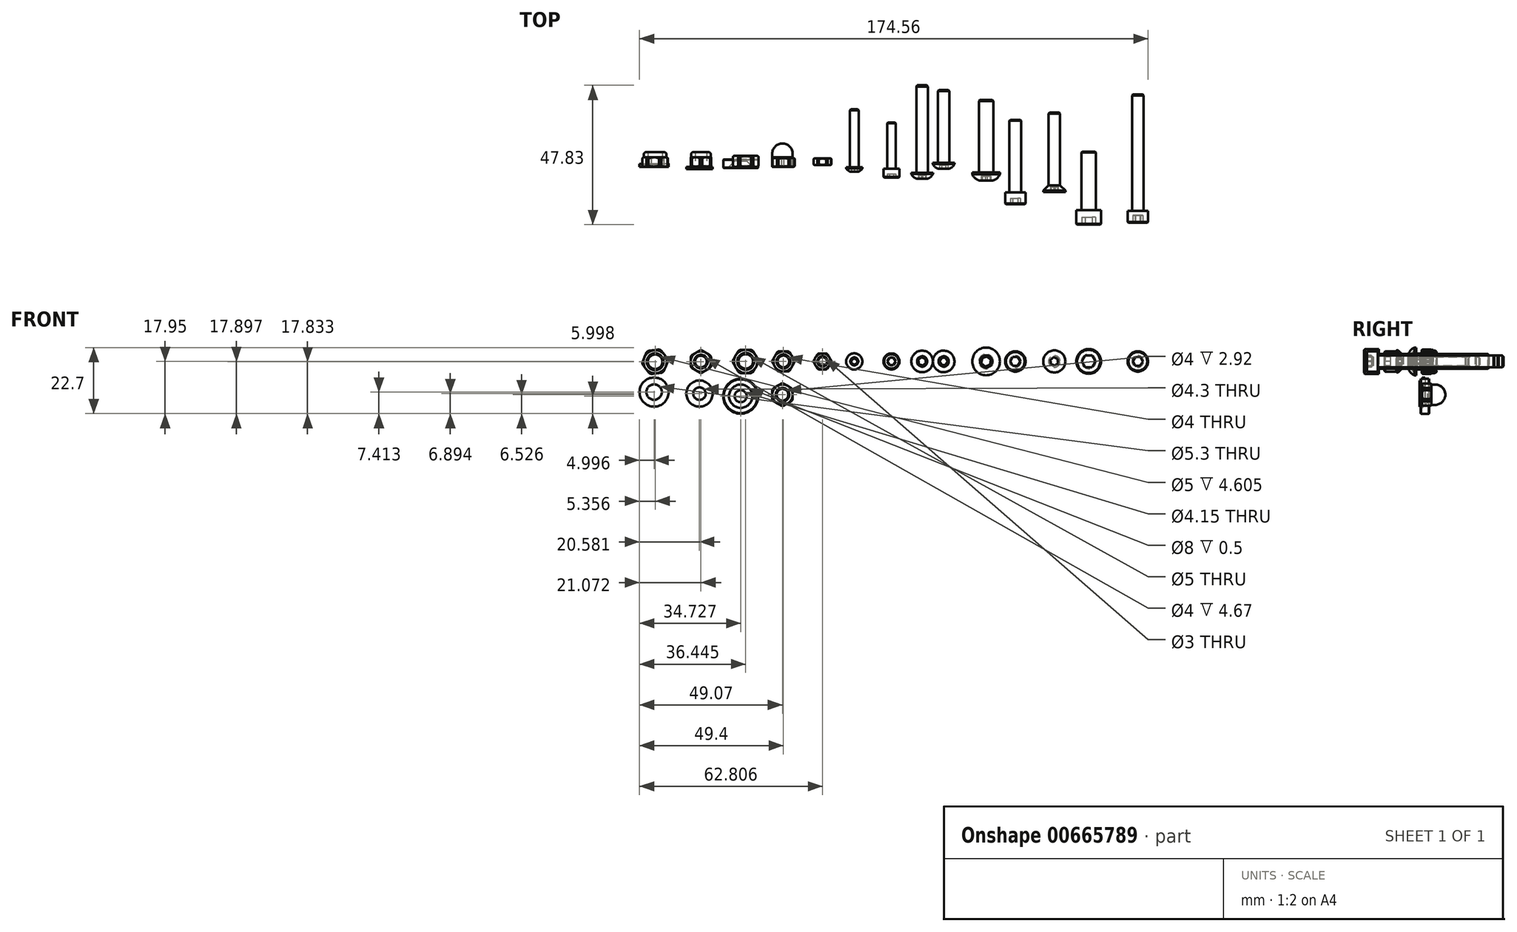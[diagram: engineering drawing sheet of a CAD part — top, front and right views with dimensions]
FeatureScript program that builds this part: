
annotation { "Feature Type Name" : "Feature", "Feature Type Description" : "" }
export const myFeature = defineFeature(function(context is Context, id is Id, definition is map)
    precondition{}
    {
        {
            var Q0;
            Q0=qCreatedBy(makeId("Top.planeOp"),FACE);
            var sketch = newSketch(context, id + "F0", { "sketchPlane" : qUnion([Q0])});
            skLineSegment(sketch, "E0.bottom", {"start": v(-2, 0) * mm, "end": v(-3.83, 0) * mm});
            skLineSegment(sketch, "E0.top", {"start": v(-2, 3) * mm, "end": v(-3.83, 3) * mm});
            skLineSegment(sketch, "E0.left", {"start": v(-2, 0) * mm, "end": v(-2, 3) * mm});
            skLineSegment(sketch, "E0.right", {"start": v(-3.83, 0) * mm, "end": v(-3.83, 3) * mm});
            skLineSegment(sketch, "E1", {"start": v(-2, 0) * mm, "end": v(0, 0) * mm, "construction": true});
            skLineSegment(sketch, "E2", {"start": v(0, 0) * mm, "end": v(0, 3) * mm, "construction": true});
            skSolve(sketch);
        }
        {
            var Q0;
            Q0=qSketchRegion(id+"F0",true);
            var Q1;
            Q1=sQuery(id+"F0.wireOp",EDGE,"E2");
            revolve(context, id + "F1", {"entities" : qUnion([Q0]), "axis" : qUnion([Q1]), "revolveType" : RevolveType.FULL});
        }
        {
            var Q0;
            Q0=makeQuery(id+"F1.opRevolve","SWEPT_EDGE",EDGE,{"disambiguationData":[OSD([sQuery(id+"F0.wireOp",EDGE,"E0.bottom"),sQuery(id+"F0.wireOp",EDGE,"E0.right")])]});
            var Q1;
            Q1=makeQuery(id+"F1.opRevolve","SWEPT_EDGE",EDGE,{"disambiguationData":[OSD([sQuery(id+"F0.wireOp",EDGE,"E0.top"),sQuery(id+"F0.wireOp",EDGE,"E0.right")])]});
            var Q2;
            Q2=makeQuery(id+"F1.opRevolve","SWEPT_EDGE",EDGE,{"disambiguationData":[OSD([sQuery(id+"F0.wireOp",EDGE,"E0.bottom"),sQuery(id+"F0.wireOp",EDGE,"E0.left")])]});
            var Q3;
            Q3=makeQuery(id+"F1.opRevolve","SWEPT_EDGE",EDGE,{"disambiguationData":[OSD([sQuery(id+"F0.wireOp",EDGE,"E0.top"),sQuery(id+"F0.wireOp",EDGE,"E0.left")])]});
            chamfer(context, id + "F2", {"entities" : qUnion([Q0, Q1, Q2, Q3]), "chamferType" : ChamferType.OFFSET_ANGLE, "width" : 0.77 * mm / 2, "oppositeDirection" : false, "angle" : 30 * degree, "tangentPropagation" : true});
        }
        {
            var Q0;
            Q0=makeQuery(id+"F1.opRevolve","SWEPT_FACE",FACE,{"disambiguationData":[OSD([sQuery(id+"F0.wireOp",EDGE,"E0.bottom")])]});
            var sketch = newSketch(context, id + "F3", { "sketchPlane" : qUnion([Q0])});
            skCircle(sketch, "E3.cCircle", {"center": v(0, 0) * mm, "radius": 3.45 * mm, "construction": true});
            skLineSegment(sketch, "E3.0", {"start": v(3.98, 0) * mm, "end": v(2, -3.45) * mm});
            skLineSegment(sketch, "E3.1", {"start": v(2, -3.45) * mm, "end": v(-2, -3.45) * mm});
            skLineSegment(sketch, "E3.2", {"start": v(-2, -3.45) * mm, "end": v(-3.98, 0) * mm});
            skLineSegment(sketch, "E3.3", {"start": v(-3.98, 0) * mm, "end": v(-2, 3.45) * mm});
            skLineSegment(sketch, "E3.4", {"start": v(-2, 3.45) * mm, "end": v(2, 3.45) * mm});
            skLineSegment(sketch, "E3.5", {"start": v(2, 3.45) * mm, "end": v(3.98, 0) * mm});
            skPoint(sketch, "E3.0.midPoint", {"position": v(2.99, -1.73) * mm});
            skCircle(sketch, "E4", {"center": v(0, 0) * mm, "radius": 4.53 * mm});
            skSolve(sketch);
        }
        {
            var Q0;
            Q0=qSketchRegion(id+"F3",true);
            extrude(context, id + "F4", {"entities" : qUnion([Q0]), "operationType" : NewBodyOperationType.REMOVE, "oppositeDirection" : true, "depth" : 25 * mm, "offsetDistance" : 25 * mm});
        }
        {
            var Q0;
            Q0=qCreatedBy(makeId("Top.planeOp"),FACE);
            var sketch = newSketch(context, id + "F5", { "sketchPlane" : qUnion([Q0])});
            skLineSegment(sketch, "E5.bottom", {"start": v(10.4, 2.85) * mm, "end": v(11.9, 2.85) * mm});
            skLineSegment(sketch, "E5.top", {"start": v(10.4, 0.58) * mm, "end": v(11.9, 0.58) * mm});
            skLineSegment(sketch, "E5.left", {"start": v(10.4, 2.85) * mm, "end": v(10.4, 0.58) * mm});
            skLineSegment(sketch, "E5.right", {"start": v(11.9, 2.85) * mm, "end": v(11.9, 0.58) * mm});
            skLineSegment(sketch, "E6", {"start": v(11.9, 0.58) * mm, "end": v(13.4, 0.58) * mm, "construction": true});
            skLineSegment(sketch, "E7", {"start": v(13.4, 0.58) * mm, "end": v(13.4, 2.85) * mm, "construction": true});
            skSolve(sketch);
        }
        {
            var Q0;
            Q0=qSketchRegion(id+"F5",true);
            var Q1;
            Q1=sQuery(id+"F5.wireOp",EDGE,"E7");
            revolve(context, id + "F6", {"entities" : qUnion([Q0]), "axis" : qUnion([Q1]), "revolveType" : RevolveType.FULL});
        }
        {
            var Q0;
            Q0=makeQuery(id+"F6.opRevolve","SWEPT_EDGE",EDGE,{"disambiguationData":[OSD([sQuery(id+"F5.wireOp",EDGE,"E5.top"),sQuery(id+"F5.wireOp",EDGE,"E5.right")])]});
            var Q1;
            Q1=makeQuery(id+"F6.opRevolve","SWEPT_EDGE",EDGE,{"disambiguationData":[OSD([sQuery(id+"F5.wireOp",EDGE,"E5.top"),sQuery(id+"F5.wireOp",EDGE,"E5.left")])]});
            var Q2;
            Q2=makeQuery(id+"F6.opRevolve","SWEPT_EDGE",EDGE,{"disambiguationData":[OSD([sQuery(id+"F5.wireOp",EDGE,"E5.bottom"),sQuery(id+"F5.wireOp",EDGE,"E5.right")])]});
            var Q3;
            Q3=makeQuery(id+"F6.opRevolve","SWEPT_EDGE",EDGE,{"disambiguationData":[OSD([sQuery(id+"F5.wireOp",EDGE,"E5.bottom"),sQuery(id+"F5.wireOp",EDGE,"E5.left")])]});
            chamfer(context, id + "F7", {"entities" : qUnion([Q0, Q1, Q2, Q3]), "width" : 0.51 / 2 * mm, "tangentPropagation" : true});
        }
        {
            var Q0;
            Q0=makeQuery(id+"F6.opRevolve","SWEPT_FACE",FACE,{"disambiguationData":[OSD([sQuery(id+"F5.wireOp",EDGE,"E5.top")])]});
            var sketch = newSketch(context, id + "F8", { "sketchPlane" : qUnion([Q0])});
            skCircle(sketch, "E8.cCircle", {"center": v(13.4, 0) * mm, "radius": 2.75 * mm, "construction": true});
            skLineSegment(sketch, "E8.0", {"start": v(16.58, 0) * mm, "end": v(15, -2.75) * mm});
            skLineSegment(sketch, "E8.1", {"start": v(15, -2.75) * mm, "end": v(11.82, -2.75) * mm});
            skLineSegment(sketch, "E8.2", {"start": v(11.82, -2.75) * mm, "end": v(10.23, 0) * mm});
            skLineSegment(sketch, "E8.3", {"start": v(10.23, 0) * mm, "end": v(11.82, 2.75) * mm});
            skLineSegment(sketch, "E8.4", {"start": v(11.82, 2.75) * mm, "end": v(15, 2.75) * mm});
            skLineSegment(sketch, "E8.5", {"start": v(15, 2.75) * mm, "end": v(16.58, 0) * mm});
            skPoint(sketch, "E8.0.midPoint", {"position": v(15.79, -1.38) * mm});
            skCircle(sketch, "E9", {"center": v(13.4, 0) * mm, "radius": 3.66 * mm});
            skSolve(sketch);
        }
        {
            var Q0;
            Q0=qSketchRegion(id+"F8",true);
            extrude(context, id + "F9", {"entities" : qUnion([Q0]), "operationType" : NewBodyOperationType.REMOVE, "oppositeDirection" : true, "depth" : 25 * mm, "offsetDistance" : 25 * mm});
        }
        {
            var Q0;
            Q0=qCreatedBy(makeId("Top.planeOp"),FACE);
            var sketch = newSketch(context, id + "F10", { "sketchPlane" : qUnion([Q0])});
            skLineSegment(sketch, "E10.bottom", {"start": v(-15.45, 3.8) * mm, "end": v(-17.35, 3.8) * mm});
            skLineSegment(sketch, "E10.top", {"start": v(-15.45, -0.05) * mm, "end": v(-17.35, -0.05) * mm});
            skLineSegment(sketch, "E10.left", {"start": v(-15.45, 3.8) * mm, "end": v(-15.45, -0.05) * mm});
            skLineSegment(sketch, "E10.right", {"start": v(-17.35, 3.8) * mm, "end": v(-17.35, -0.05) * mm});
            skLineSegment(sketch, "E11", {"start": v(-15.45, 3.8) * mm, "end": v(-12.95, 3.8) * mm, "construction": true});
            skLineSegment(sketch, "E12", {"start": v(-12.95, 3.8) * mm, "end": v(-12.95, -0.05) * mm, "construction": true});
            skSolve(sketch);
        }
        {
            var Q0;
            Q0=qSketchRegion(id+"F10",true);
            var Q1;
            Q1=sQuery(id+"F10.wireOp",EDGE,"E12");
            revolve(context, id + "F11", {"entities" : qUnion([Q0]), "axis" : qUnion([Q1]), "revolveType" : RevolveType.FULL});
        }
        {
            var Q0;
            Q0=makeQuery(id+"F11.opRevolve","SWEPT_EDGE",EDGE,{"disambiguationData":[OSD([sQuery(id+"F10.wireOp",EDGE,"E10.bottom"),sQuery(id+"F10.wireOp",EDGE,"E10.left")])]});
            var Q1;
            Q1=makeQuery(id+"F11.opRevolve","SWEPT_EDGE",EDGE,{"disambiguationData":[OSD([sQuery(id+"F10.wireOp",EDGE,"E10.bottom"),sQuery(id+"F10.wireOp",EDGE,"E10.right")])]});
            var Q2;
            Q2=makeQuery(id+"F11.opRevolve","SWEPT_EDGE",EDGE,{"disambiguationData":[OSD([sQuery(id+"F10.wireOp",EDGE,"E10.top"),sQuery(id+"F10.wireOp",EDGE,"E10.left")])]});
            var Q3;
            Q3=makeQuery(id+"F11.opRevolve","SWEPT_EDGE",EDGE,{"disambiguationData":[OSD([sQuery(id+"F10.wireOp",EDGE,"E10.top"),sQuery(id+"F10.wireOp",EDGE,"E10.right")])]});
            chamfer(context, id + "F12", {"entities" : qUnion([Q0, Q1, Q2, Q3]), "width" : 0.4 * mm, "tangentPropagation" : true});
        }
        {
            var Q0;
            Q0=makeQuery(id+"F11.opRevolve","SWEPT_FACE",FACE,{"disambiguationData":[OSD([sQuery(id+"F10.wireOp",EDGE,"E10.top")])]});
            var sketch = newSketch(context, id + "F13", { "sketchPlane" : qUnion([Q0])});
            skCircle(sketch, "E13.cCircle", {"center": v(-12.95, 0) * mm, "radius": 4 * mm, "construction": true});
            skLineSegment(sketch, "E13.0", {"start": v(-8.34, 0) * mm, "end": v(-10.65, -4) * mm});
            skLineSegment(sketch, "E13.1", {"start": v(-10.65, -4) * mm, "end": v(-15.26, -4) * mm});
            skLineSegment(sketch, "E13.2", {"start": v(-15.26, -4) * mm, "end": v(-17.57, 0) * mm});
            skLineSegment(sketch, "E13.3", {"start": v(-17.57, 0) * mm, "end": v(-15.26, 4) * mm});
            skLineSegment(sketch, "E13.4", {"start": v(-15.26, 4) * mm, "end": v(-10.65, 4) * mm});
            skLineSegment(sketch, "E13.5", {"start": v(-10.65, 4) * mm, "end": v(-8.34, 0) * mm});
            skPoint(sketch, "E13.0.midPoint", {"position": v(-9.5, -2) * mm});
            skCircle(sketch, "E14", {"center": v(-12.95, 0) * mm, "radius": 5.32 * mm});
            skSolve(sketch);
        }
        {
            var Q0;
            Q0=qSketchRegion(id+"F13",true);
            extrude(context, id + "F14", {"entities" : qUnion([Q0]), "operationType" : NewBodyOperationType.REMOVE, "oppositeDirection" : true, "depth" : 25 * mm, "offsetDistance" : 25 * mm});
        }
        {
            var Q0;
            Q0=qCreatedBy(makeId("Top.planeOp"),FACE);
            var sketch = newSketch(context, id + "F15", { "sketchPlane" : qUnion([Q0])});
            skLineSegment(sketch, "E15", {"start": v(24.32, 19.82) * mm, "end": v(24.32, -1.7) * mm});
            skLineSegment(sketch, "E16", {"start": v(24.32, -1.7) * mm, "end": v(22.95, -1.7) * mm});
            skLineSegment(sketch, "E17", {"start": v(21.55, -0.58) * mm, "end": v(21.55, -0.18) * mm});
            skLineSegment(sketch, "E18", {"start": v(21.55, -0.18) * mm, "end": v(22.82, -0.18) * mm});
            skLineSegment(sketch, "E19", {"start": v(22.82, -0.18) * mm, "end": v(22.82, 19.41) * mm});
            skLineSegment(sketch, "E20", {"start": v(22.82, 19.41) * mm, "end": v(23.18, 19.82) * mm});
            skLineSegment(sketch, "E21", {"start": v(23.18, 19.82) * mm, "end": v(24.32, 19.82) * mm});
            skArc(sketch, "E22", {"start": v(22.95, -1.7) * mm, "mid": v(22.16, -1.26) * mm, "end": v(21.55, -0.58) * mm});
            skSolve(sketch);
        }
        {
            var Q0;
            Q0=qSketchRegion(id+"F15",true);
            var Q1;
            Q1=sQuery(id+"F15.wireOp",EDGE,"E15");
            revolve(context, id + "F16", {"entities" : qUnion([Q0]), "axis" : qUnion([Q1]), "revolveType" : RevolveType.FULL});
        }
        {
            var Q0;
            Q0=makeQuery(id+"F16.opRevolve","SWEPT_FACE",FACE,{"disambiguationData":[OSD([sQuery(id+"F15.wireOp",EDGE,"E16")])]});
            var sketch = newSketch(context, id + "F17", { "sketchPlane" : qUnion([Q0])});
            skCircle(sketch, "E23.cCircle", {"center": v(24.32, 0) * mm, "radius": 1.02 * mm, "construction": true});
            skLineSegment(sketch, "E23.0", {"start": v(25.34, 0.59) * mm, "end": v(25.34, -0.59) * mm});
            skLineSegment(sketch, "E23.1", {"start": v(25.34, -0.59) * mm, "end": v(24.32, -1.17) * mm});
            skLineSegment(sketch, "E23.2", {"start": v(24.32, -1.17) * mm, "end": v(23.3, -0.59) * mm});
            skLineSegment(sketch, "E23.3", {"start": v(23.3, -0.59) * mm, "end": v(23.3, 0.59) * mm});
            skLineSegment(sketch, "E23.4", {"start": v(23.3, 0.59) * mm, "end": v(24.32, 1.17) * mm});
            skLineSegment(sketch, "E23.5", {"start": v(24.32, 1.17) * mm, "end": v(25.34, 0.59) * mm});
            skPoint(sketch, "E23.0.midPoint", {"position": v(25.34, 0) * mm});
            skSolve(sketch);
        }
        {
            var Q0;
            Q0=qSketchRegion(id+"F17",true);
            extrude(context, id + "F18", {"entities" : qUnion([Q0]), "operationType" : NewBodyOperationType.REMOVE, "oppositeDirection" : true, "depth" : 1.04 * mm, "offsetDistance" : 25 * mm});
        }
        {
            var Q0;
            Q0=qCreatedBy(makeId("Top.planeOp"),FACE);
            var sketch = newSketch(context, id + "F19", { "sketchPlane" : qUnion([Q0])});
            skLineSegment(sketch, "E24.bottom", {"start": v(34.33, -0.72) * mm, "end": v(35.58, -0.72) * mm});
            skLineSegment(sketch, "E24.top", {"start": v(34.61, -3.72) * mm, "end": v(37.08, -3.72) * mm});
            skLineSegment(sketch, "E24.left", {"start": v(34.33, -0.72) * mm, "end": v(34.33, -3.44) * mm});
            skLineSegment(sketch, "E24.right", {"start": v(37.08, -0.72) * mm, "end": v(37.08, -3.72) * mm});
            skLineSegment(sketch, "E25.top", {"start": v(37.08, 15.2) * mm, "end": v(35.86, 15.2) * mm});
            skLineSegment(sketch, "E25.left", {"start": v(37.08, -0.72) * mm, "end": v(37.08, 15.2) * mm});
            skLineSegment(sketch, "E25.right", {"start": v(35.58, -0.72) * mm, "end": v(35.58, 14.92) * mm});
            skLineSegment(sketch, "E26", {"start": v(34.33, -3.44) * mm, "end": v(34.61, -3.72) * mm});
            skLineSegment(sketch, "E27", {"start": v(35.58, 14.92) * mm, "end": v(35.86, 15.2) * mm});
            skSolve(sketch);
        }
        {
            var Q0;
            Q0=qSketchRegion(id+"F19",true);
            var Q1;
            Q1=sQuery(id+"F19.wireOp",EDGE,"E25.left");
            revolve(context, id + "F20", {"entities" : qUnion([Q0]), "axis" : qUnion([Q1]), "revolveType" : RevolveType.FULL});
        }
        {
            var Q0;
            Q0=makeQuery(id+"F20.opRevolve","SWEPT_FACE",FACE,{"disambiguationData":[OSD([sQuery(id+"F19.wireOp",EDGE,"E24.top")])]});
            var sketch = newSketch(context, id + "F21", { "sketchPlane" : qUnion([Q0])});
            skCircle(sketch, "E28.cCircle", {"center": v(37.08, 0) * mm, "radius": 1.25 * mm, "construction": true});
            skLineSegment(sketch, "E28.0", {"start": v(37.8, 1.25) * mm, "end": v(38.52, 0) * mm});
            skLineSegment(sketch, "E28.1", {"start": v(38.52, 0) * mm, "end": v(37.8, -1.25) * mm});
            skLineSegment(sketch, "E28.2", {"start": v(37.8, -1.25) * mm, "end": v(36.36, -1.25) * mm});
            skLineSegment(sketch, "E28.3", {"start": v(36.36, -1.25) * mm, "end": v(35.64, 0) * mm});
            skLineSegment(sketch, "E28.4", {"start": v(35.64, 0) * mm, "end": v(36.36, 1.25) * mm});
            skLineSegment(sketch, "E28.5", {"start": v(36.36, 1.25) * mm, "end": v(37.8, 1.25) * mm});
            skPoint(sketch, "E28.0.midPoint", {"position": v(38.16, 0.62) * mm});
            skSolve(sketch);
        }
        {
            var Q0;
            Q0=qSketchRegion(id+"F21",true);
            extrude(context, id + "F22", {"entities" : qUnion([Q0]), "operationType" : NewBodyOperationType.REMOVE, "oppositeDirection" : true, "depth" : 1.3 * mm, "offsetDistance" : 25 * mm});
        }
        {
            var Q0;
            Q0=qCreatedBy(makeId("Top.planeOp"),FACE);
            var sketch = newSketch(context, id + "F23", { "sketchPlane" : qUnion([Q0])});
            skLineSegment(sketch, "E29", {"start": v(55, 26.35) * mm, "end": v(55, -0.73) * mm});
            skLineSegment(sketch, "E30", {"start": v(55, -0.73) * mm, "end": v(53.25, -0.73) * mm});
            skLineSegment(sketch, "E31", {"start": v(51.3, 0.95) * mm, "end": v(51.3, 1.35) * mm});
            skLineSegment(sketch, "E32", {"start": v(51.3, 1.35) * mm, "end": v(53, 1.35) * mm});
            skLineSegment(sketch, "E33", {"start": v(53, 1.35) * mm, "end": v(53, 25.94) * mm});
            skLineSegment(sketch, "E34", {"start": v(53, 25.94) * mm, "end": v(53.36, 26.35) * mm});
            skLineSegment(sketch, "E35", {"start": v(53.36, 26.35) * mm, "end": v(55, 26.35) * mm});
            skArc(sketch, "E36", {"start": v(53.25, -0.73) * mm, "mid": v(52.07, -0.12) * mm, "end": v(51.3, 0.95) * mm});
            skSolve(sketch);
        }
        {
            var Q0;
            Q0=qSketchRegion(id+"F23",true);
            var Q1;
            Q1=sQuery(id+"F23.wireOp",EDGE,"E29");
            revolve(context, id + "F24", {"entities" : qUnion([Q0]), "axis" : qUnion([Q1]), "revolveType" : RevolveType.FULL});
        }
        {
            var Q0;
            Q0=makeQuery(id+"F24.opRevolve","SWEPT_FACE",FACE,{"disambiguationData":[OSD([sQuery(id+"F23.wireOp",EDGE,"E30")])]});
            var sketch = newSketch(context, id + "F25", { "sketchPlane" : qUnion([Q0])});
            skCircle(sketch, "E37.cCircle", {"center": v(55, 0) * mm, "radius": 1.27 * mm, "construction": true});
            skLineSegment(sketch, "E37.0", {"start": v(56.47, 0) * mm, "end": v(55.73, -1.27) * mm});
            skLineSegment(sketch, "E37.1", {"start": v(55.73, -1.27) * mm, "end": v(54.27, -1.27) * mm});
            skLineSegment(sketch, "E37.2", {"start": v(54.27, -1.27) * mm, "end": v(53.53, 0) * mm});
            skLineSegment(sketch, "E37.3", {"start": v(53.53, 0) * mm, "end": v(54.27, 1.27) * mm});
            skLineSegment(sketch, "E37.4", {"start": v(54.27, 1.27) * mm, "end": v(55.73, 1.27) * mm});
            skLineSegment(sketch, "E37.5", {"start": v(55.73, 1.27) * mm, "end": v(56.47, 0) * mm});
            skPoint(sketch, "E37.0.midPoint", {"position": v(56.1, -0.64) * mm});
            skSolve(sketch);
        }
        {
            var Q0;
            Q0=qSketchRegion(id+"F25",true);
            extrude(context, id + "F26", {"entities" : qUnion([Q0]), "operationType" : NewBodyOperationType.REMOVE, "oppositeDirection" : true, "depth" : 1.3 * mm, "offsetDistance" : 25 * mm});
        }
        {
            var Q0;
            Q0=qCreatedBy(makeId("Top.planeOp"),FACE);
            var sketch = newSketch(context, id + "F27", { "sketchPlane" : qUnion([Q0])});
            skLineSegment(sketch, "E38.bottom", {"start": v(76.11, -8.88) * mm, "end": v(77.61, -8.88) * mm});
            skLineSegment(sketch, "E38.top", {"start": v(76.4, -12.88) * mm, "end": v(79.61, -12.88) * mm});
            skLineSegment(sketch, "E38.left", {"start": v(76.11, -8.88) * mm, "end": v(76.11, -12.6) * mm});
            skLineSegment(sketch, "E38.right", {"start": v(79.61, -8.88) * mm, "end": v(79.61, -12.88) * mm});
            skLineSegment(sketch, "E39.top", {"start": v(79.61, 16.12) * mm, "end": v(77.9, 16.12) * mm});
            skLineSegment(sketch, "E39.left", {"start": v(79.61, -8.88) * mm, "end": v(79.61, 16.12) * mm});
            skLineSegment(sketch, "E39.right", {"start": v(77.61, -8.88) * mm, "end": v(77.61, 15.84) * mm});
            skLineSegment(sketch, "E40", {"start": v(76.11, -12.6) * mm, "end": v(76.4, -12.88) * mm});
            skLineSegment(sketch, "E41", {"start": v(77.61, 15.84) * mm, "end": v(77.9, 16.12) * mm});
            skSolve(sketch);
        }
        {
            var Q0;
            Q0=qSketchRegion(id+"F27",true);
            var Q1;
            Q1=sQuery(id+"F27.wireOp",EDGE,"E39.left");
            revolve(context, id + "F28", {"entities" : qUnion([Q0]), "axis" : qUnion([Q1]), "revolveType" : RevolveType.FULL});
        }
        {
            var Q0;
            Q0=makeQuery(id+"F28.opRevolve","SWEPT_FACE",FACE,{"disambiguationData":[OSD([sQuery(id+"F27.wireOp",EDGE,"E38.top")])]});
            var sketch = newSketch(context, id + "F29", { "sketchPlane" : qUnion([Q0])});
            skCircle(sketch, "E42.cCircle", {"center": v(79.61, 0) * mm, "radius": 1.5 * mm, "construction": true});
            skLineSegment(sketch, "E42.0", {"start": v(81.34, 0) * mm, "end": v(80.48, -1.5) * mm});
            skLineSegment(sketch, "E42.1", {"start": v(80.48, -1.5) * mm, "end": v(78.75, -1.5) * mm});
            skLineSegment(sketch, "E42.2", {"start": v(78.75, -1.5) * mm, "end": v(77.88, 0) * mm});
            skLineSegment(sketch, "E42.3", {"start": v(77.88, 0) * mm, "end": v(78.75, 1.5) * mm});
            skLineSegment(sketch, "E42.4", {"start": v(78.75, 1.5) * mm, "end": v(80.48, 1.5) * mm});
            skLineSegment(sketch, "E42.5", {"start": v(80.48, 1.5) * mm, "end": v(81.34, 0) * mm});
            skPoint(sketch, "E42.0.midPoint", {"position": v(80.91, -0.75) * mm});
            skSolve(sketch);
        }
        {
            var Q0;
            Q0=qSketchRegion(id+"F29",true);
            extrude(context, id + "F30", {"entities" : qUnion([Q0]), "operationType" : NewBodyOperationType.REMOVE, "oppositeDirection" : true, "depth" : 2 * mm, "offsetDistance" : 25 * mm});
        }
        {
            var Q0;
            Q0=qCreatedBy(makeId("Top.planeOp"),FACE);
            var sketch = newSketch(context, id + "F31", { "sketchPlane" : qUnion([Q0])});
            skLineSegment(sketch, "E43.bottom", {"start": v(100.55, -14.88) * mm, "end": v(102.3, -14.88) * mm});
            skLineSegment(sketch, "E43.top", {"start": v(100.83, -19.88) * mm, "end": v(104.8, -19.88) * mm});
            skLineSegment(sketch, "E43.left", {"start": v(100.55, -14.88) * mm, "end": v(100.55, -19.6) * mm});
            skLineSegment(sketch, "E43.right", {"start": v(104.8, -14.88) * mm, "end": v(104.8, -19.88) * mm});
            skLineSegment(sketch, "E44.top", {"start": v(104.8, 5.12) * mm, "end": v(102.58, 5.12) * mm});
            skLineSegment(sketch, "E44.left", {"start": v(104.8, -14.88) * mm, "end": v(104.8, 5.12) * mm});
            skLineSegment(sketch, "E44.right", {"start": v(102.3, -14.88) * mm, "end": v(102.3, 4.84) * mm});
            skLineSegment(sketch, "E45", {"start": v(100.55, -19.6) * mm, "end": v(100.83, -19.88) * mm});
            skLineSegment(sketch, "E46", {"start": v(102.3, 4.84) * mm, "end": v(102.58, 5.12) * mm});
            skSolve(sketch);
        }
        {
            var Q0;
            Q0=qSketchRegion(id+"F31",true);
            var Q1;
            Q1=sQuery(id+"F31.wireOp",EDGE,"E43.right");
            revolve(context, id + "F32", {"entities" : qUnion([Q0]), "axis" : qUnion([Q1]), "revolveType" : RevolveType.FULL});
        }
        {
            var Q0;
            Q0=makeQuery(id+"F32.opRevolve","SWEPT_FACE",FACE,{"disambiguationData":[OSD([sQuery(id+"F31.wireOp",EDGE,"E43.top")])]});
            var sketch = newSketch(context, id + "F33", { "sketchPlane" : qUnion([Q0])});
            skCircle(sketch, "E47.cCircle", {"center": v(104.8, 0) * mm, "radius": 2 * mm, "construction": true});
            skLineSegment(sketch, "E47.0", {"start": v(107.1, 0) * mm, "end": v(105.95, -2) * mm});
            skLineSegment(sketch, "E47.1", {"start": v(105.95, -2) * mm, "end": v(103.64, -2) * mm});
            skLineSegment(sketch, "E47.2", {"start": v(103.64, -2) * mm, "end": v(102.49, 0) * mm});
            skLineSegment(sketch, "E47.3", {"start": v(102.49, 0) * mm, "end": v(103.64, 2) * mm});
            skLineSegment(sketch, "E47.4", {"start": v(103.64, 2) * mm, "end": v(105.95, 2) * mm});
            skLineSegment(sketch, "E47.5", {"start": v(105.95, 2) * mm, "end": v(107.1, 0) * mm});
            skPoint(sketch, "E47.0.midPoint", {"position": v(106.53, -1) * mm});
            skSolve(sketch);
        }
        {
            var Q0;
            Q0=qSketchRegion(id+"F33",true);
            extrude(context, id + "F34", {"entities" : qUnion([Q0]), "operationType" : NewBodyOperationType.REMOVE, "oppositeDirection" : true, "depth" : 2.5 * mm, "offsetDistance" : 25 * mm});
        }
        {
            var Q0;
            Q0=qCreatedBy(makeId("Top.planeOp"),FACE);
            var sketch = newSketch(context, id + "F35", { "sketchPlane" : qUnion([Q0])});
            skLineSegment(sketch, "E48.bottom", {"start": v(118.16, -15.2) * mm, "end": v(119.66, -15.2) * mm});
            skLineSegment(sketch, "E48.top", {"start": v(118.45, -19.2) * mm, "end": v(121.66, -19.2) * mm});
            skLineSegment(sketch, "E48.left", {"start": v(118.16, -15.2) * mm, "end": v(118.16, -18.93) * mm});
            skLineSegment(sketch, "E48.right", {"start": v(121.66, -15.2) * mm, "end": v(121.66, -19.2) * mm});
            skLineSegment(sketch, "E49.top", {"start": v(121.66, 24.8) * mm, "end": v(119.95, 24.8) * mm});
            skLineSegment(sketch, "E49.left", {"start": v(121.66, -15.2) * mm, "end": v(121.66, 24.8) * mm});
            skLineSegment(sketch, "E49.right", {"start": v(119.66, -15.2) * mm, "end": v(119.66, 24.5) * mm});
            skLineSegment(sketch, "E50", {"start": v(118.16, -18.93) * mm, "end": v(118.45, -19.2) * mm});
            skLineSegment(sketch, "E51", {"start": v(119.66, 24.5) * mm, "end": v(119.95, 24.8) * mm});
            skSolve(sketch);
        }
        {
            var Q0;
            Q0=qSketchRegion(id+"F35",true);
            var Q1;
            Q1=sQuery(id+"F35.wireOp",EDGE,"E49.left");
            revolve(context, id + "F36", {"entities" : qUnion([Q0]), "axis" : qUnion([Q1]), "revolveType" : RevolveType.FULL});
        }
        {
            var Q0;
            Q0=makeQuery(id+"F36.opRevolve","SWEPT_FACE",FACE,{"disambiguationData":[OSD([sQuery(id+"F35.wireOp",EDGE,"E48.top")])]});
            var sketch = newSketch(context, id + "F37", { "sketchPlane" : qUnion([Q0])});
            skCircle(sketch, "E52.cCircle", {"center": v(121.66, 0) * mm, "radius": 1.5 * mm, "construction": true});
            skLineSegment(sketch, "E52.0", {"start": v(122.62, 1.44) * mm, "end": v(123.4, -0.1) * mm});
            skLineSegment(sketch, "E52.1", {"start": v(123.4, -0.1) * mm, "end": v(122.43, -1.55) * mm});
            skLineSegment(sketch, "E52.2", {"start": v(122.43, -1.55) * mm, "end": v(120.7, -1.44) * mm});
            skLineSegment(sketch, "E52.3", {"start": v(120.7, -1.44) * mm, "end": v(119.94, 0.1) * mm});
            skLineSegment(sketch, "E52.4", {"start": v(119.94, 0.1) * mm, "end": v(120.9, 1.55) * mm});
            skLineSegment(sketch, "E52.5", {"start": v(120.9, 1.55) * mm, "end": v(122.62, 1.44) * mm});
            skPoint(sketch, "E52.0.midPoint", {"position": v(123, 0.67) * mm});
            skSolve(sketch);
        }
        {
            var Q0;
            Q0=qSketchRegion(id+"F37",true);
            extrude(context, id + "F38", {"entities" : qUnion([Q0]), "operationType" : NewBodyOperationType.REMOVE, "oppositeDirection" : true, "depth" : 2.5 * mm, "offsetDistance" : 25 * mm});
        }
        {
            var Q0;
            Q0=qCreatedBy(makeId("Front.planeOp"),FACE);
            var sketch = newSketch(context, id + "F39", { "sketchPlane" : qUnion([Q0])});
            skCircle(sketch, "E53", {"center": v(-28.33, -0.05) * mm, "radius": 3.83 * mm});
            skCircle(sketch, "E54", {"center": v(-28.33, -0.05) * mm, "radius": 2 * mm});
            skSolve(sketch);
        }
        {
            var Q0;
            Q0=qSketchRegion(id+"F39",true);
            extrude(context, id + "F40", {"entities" : qUnion([Q0]), "oppositeDirection" : true, "depth" : 3.25 * mm, "offsetDistance" : 25 * mm});
        }
        {
            var Q0;
            Q0=makeQuery(id+"F40.opExtrude","CAP_EDGE",EDGE,{"disambiguationData":[OSD([sQuery(id+"F39.wireOp",EDGE,"E53")])],"isStart":false});
            var Q1;
            Q1=makeQuery(id+"F40.opExtrude","CAP_EDGE",EDGE,{"disambiguationData":[OSD([sQuery(id+"F39.wireOp",EDGE,"E53")])],"isStart":true});
            var Q2;
            Q2=makeQuery(id+"F40.opExtrude","CAP_EDGE",EDGE,{"disambiguationData":[OSD([sQuery(id+"F39.wireOp",EDGE,"E54")])],"isStart":true});
            chamfer(context, id + "F41", {"entities" : qUnion([Q0, Q1, Q2]), "width" : 0.66 / 2 * mm, "tangentPropagation" : true});
        }
        {
            var Q0;
            Q0=makeQuery(id+"F40.opExtrude","CAP_FACE",FACE,{"disambiguationData":[OSD([sQuery(id+"F39.wireOp",EDGE,"E53"),sQuery(id+"F39.wireOp",EDGE,"E54")])],"isStart":false});
            var sketch = newSketch(context, id + "F42", { "sketchPlane" : qUnion([Q0])});
            skCircle(sketch, "E55.cCircle", {"center": v(28.33, -0.05) * mm, "radius": 3.5 * mm, "construction": true});
            skLineSegment(sketch, "E55.0", {"start": v(31.83, 1.97) * mm, "end": v(31.83, -2.07) * mm});
            skLineSegment(sketch, "E55.1", {"start": v(31.83, -2.07) * mm, "end": v(28.33, -4.1) * mm});
            skLineSegment(sketch, "E55.2", {"start": v(28.33, -4.1) * mm, "end": v(24.83, -2.07) * mm});
            skLineSegment(sketch, "E55.3", {"start": v(24.83, -2.07) * mm, "end": v(24.83, 1.97) * mm});
            skLineSegment(sketch, "E55.4", {"start": v(24.83, 1.97) * mm, "end": v(28.33, 3.99) * mm});
            skLineSegment(sketch, "E55.5", {"start": v(28.33, 3.99) * mm, "end": v(31.83, 1.97) * mm});
            skPoint(sketch, "E55.0.midPoint", {"position": v(31.83, -0.05) * mm});
            skCircle(sketch, "E56", {"center": v(28.33, -0.05) * mm, "radius": 6.48 * mm});
            skSolve(sketch);
        }
        {
            var Q0;
            Q0=qSketchRegion(id+"F42",true);
            extrude(context, id + "F43", {"entities" : qUnion([Q0]), "operationType" : NewBodyOperationType.REMOVE, "oppositeDirection" : true, "depth" : 25 * mm, "offsetDistance" : 25 * mm});
        }
        {
            var Q0;
            Q0=makeQuery(id+"F40.opExtrude","CAP_FACE",FACE,{"disambiguationData":[OSD([sQuery(id+"F39.wireOp",EDGE,"E53"),sQuery(id+"F39.wireOp",EDGE,"E54")])],"isStart":false});
            var sketch = newSketch(context, id + "F44", { "sketchPlane" : qUnion([Q0])});
            skCircle(sketch, "E57", {"center": v(28.33, -0.05) * mm, "radius": 2 * mm});
            skCircle(sketch, "E58", {"center": v(28.33, -0.05) * mm, "radius": 3.38 * mm});
            skSolve(sketch);
        }
        {
            var Q0;
            Q0=qSketchRegion(id+"F44",true);
            extrude(context, id + "F45", {"entities" : qUnion([Q0]), "operationType" : NewBodyOperationType.ADD, "depth" : (5 - 3.25) * mm, "offsetDistance" : 25 * mm});
        }
        {
            var Q0;
            Q0=makeQuery(id+"F45.opExtrude","CAP_EDGE",EDGE,{"disambiguationData":[OSD([sQuery(id+"F44.wireOp",EDGE,"E58")])],"isStart":false});
            fillet(context, id + "F46", {"entities" : qUnion([Q0]), "radius" : 0.75 * mm, "tangentPropagation" : true, "allowEdgeOverflow" : false});
        }
        {
            var Q0;
            Q0=qCreatedBy(makeId("Top.planeOp"),FACE);
            var sketch = newSketch(context, id + "F47", { "sketchPlane" : qUnion([Q0])});
            skLineSegment(sketch, "E59", {"start": v(69.58, 22.98) * mm, "end": v(69.58, -4.77) * mm});
            skLineSegment(sketch, "E60", {"start": v(69.58, -4.77) * mm, "end": v(67.48, -4.77) * mm});
            skLineSegment(sketch, "E61", {"start": v(64.83, -2.62) * mm, "end": v(64.83, -2.02) * mm});
            skLineSegment(sketch, "E62", {"start": v(64.83, -2.02) * mm, "end": v(67.08, -2.02) * mm});
            skLineSegment(sketch, "E63", {"start": v(67.08, -2.02) * mm, "end": v(67.08, 22.58) * mm});
            skLineSegment(sketch, "E64", {"start": v(67.08, 22.58) * mm, "end": v(67.44, 22.98) * mm});
            skLineSegment(sketch, "E65", {"start": v(67.44, 22.98) * mm, "end": v(69.58, 22.98) * mm});
            skArc(sketch, "E66", {"start": v(67.48, -4.77) * mm, "mid": v(65.88, -4.03) * mm, "end": v(64.83, -2.62) * mm});
            skSolve(sketch);
        }
        {
            var Q0;
            Q0=makeQuery(id+"F47.imprint","IMPRINT",FACE,{"disambiguationData":[TD([[makeQuery(id+"F47.imprint","IMPRINT",EDGE,{"derivedFrom":sQuery(id+"F47.wireOp",EDGE,"E59")}),-1.0]])]});
            var Q1;
            Q1=sQuery(id+"F47.wireOp",EDGE,"E59");
            revolve(context, id + "F48", {"entities" : qUnion([Q0]), "axis" : qUnion([Q1]), "revolveType" : RevolveType.FULL});
        }
        {
            var Q0;
            Q0=makeQuery(id+"F48.opRevolve","SWEPT_FACE",FACE,{"disambiguationData":[OSD([sQuery(id+"F47.wireOp",EDGE,"E60")])]});
            var sketch = newSketch(context, id + "F49", { "sketchPlane" : qUnion([Q0])});
            skCircle(sketch, "E67.cCircle", {"center": v(69.58, 0) * mm, "radius": 1.5 * mm, "construction": true});
            skLineSegment(sketch, "E67.0", {"start": v(69.92, 1.7) * mm, "end": v(71.22, 0.55) * mm});
            skLineSegment(sketch, "E67.1", {"start": v(71.22, 0.55) * mm, "end": v(70.88, -1.14) * mm});
            skLineSegment(sketch, "E67.2", {"start": v(70.88, -1.14) * mm, "end": v(69.24, -1.7) * mm});
            skLineSegment(sketch, "E67.3", {"start": v(69.24, -1.7) * mm, "end": v(67.94, -0.55) * mm});
            skLineSegment(sketch, "E67.4", {"start": v(67.94, -0.55) * mm, "end": v(68.28, 1.14) * mm});
            skLineSegment(sketch, "E67.5", {"start": v(68.28, 1.14) * mm, "end": v(69.92, 1.7) * mm});
            skPoint(sketch, "E67.0.midPoint", {"position": v(70.57, 1.13) * mm});
            skSolve(sketch);
        }
        {
            var Q0;
            Q0=qSketchRegion(id+"F49",true);
            extrude(context, id + "F50", {"entities" : qUnion([Q0]), "operationType" : NewBodyOperationType.REMOVE, "oppositeDirection" : true, "depth" : 1.56 * mm, "offsetDistance" : 25 * mm});
        }
        {
            var Q0;
            Q0=qCreatedBy(makeId("Front.planeOp"),FACE);
            var sketch = newSketch(context, id + "F51", { "sketchPlane" : qUnion([Q0])});
            skCircle(sketch, "E68", {"center": v(-44.04, -0.12) * mm, "radius": 4.4 * mm});
            skCircle(sketch, "E69", {"center": v(-44.04, -0.12) * mm, "radius": 2.5 * mm});
            skSolve(sketch);
        }
        {
            var Q0;
            Q0=qSketchRegion(id+"F51",true);
            extrude(context, id + "F52", {"entities" : qUnion([Q0]), "oppositeDirection" : true, "depth" : 3.25 * mm, "offsetDistance" : 25 * mm});
        }
        {
            var Q0;
            Q0=makeQuery(id+"F52.opExtrude","CAP_EDGE",EDGE,{"disambiguationData":[OSD([sQuery(id+"F51.wireOp",EDGE,"E68")])],"isStart":false});
            var Q1;
            Q1=makeQuery(id+"F52.opExtrude","CAP_EDGE",EDGE,{"disambiguationData":[OSD([sQuery(id+"F51.wireOp",EDGE,"E68")])],"isStart":true});
            var Q2;
            Q2=makeQuery(id+"F52.opExtrude","CAP_EDGE",EDGE,{"disambiguationData":[OSD([sQuery(id+"F51.wireOp",EDGE,"E69")])],"isStart":true});
            chamfer(context, id + "F53", {"entities" : qUnion([Q0, Q1, Q2]), "width" : (0.79 / 2) * mm, "tangentPropagation" : true});
        }
        {
            var Q0;
            Q0=makeQuery(id+"F52.opExtrude","CAP_FACE",FACE,{"disambiguationData":[OSD([sQuery(id+"F51.wireOp",EDGE,"E68"),sQuery(id+"F51.wireOp",EDGE,"E69")])],"isStart":false});
            var sketch = newSketch(context, id + "F54", { "sketchPlane" : qUnion([Q0])});
            skCircle(sketch, "E70.cCircle", {"center": v(44.04, -0.12) * mm, "radius": 4 * mm, "construction": true});
            skLineSegment(sketch, "E70.0", {"start": v(39.46, 0.47) * mm, "end": v(42.26, 4.14) * mm});
            skLineSegment(sketch, "E70.1", {"start": v(42.26, 4.14) * mm, "end": v(46.84, 3.56) * mm});
            skLineSegment(sketch, "E70.2", {"start": v(46.84, 3.56) * mm, "end": v(48.63, -0.7) * mm});
            skLineSegment(sketch, "E70.3", {"start": v(48.63, -0.7) * mm, "end": v(45.83, -4.38) * mm});
            skLineSegment(sketch, "E70.4", {"start": v(45.83, -4.38) * mm, "end": v(41.25, -3.8) * mm});
            skLineSegment(sketch, "E70.5", {"start": v(41.25, -3.8) * mm, "end": v(39.46, 0.47) * mm});
            skPoint(sketch, "E70.0.midPoint", {"position": v(40.86, 2.3) * mm});
            skCircle(sketch, "E71", {"center": v(44.04, -0.12) * mm, "radius": 6.63 * mm});
            skSolve(sketch);
        }
        {
            var Q0;
            Q0=qSketchRegion(id+"F54",true);
            extrude(context, id + "F55", {"entities" : qUnion([Q0]), "operationType" : NewBodyOperationType.REMOVE, "oppositeDirection" : true, "depth" : 25 * mm, "offsetDistance" : 25 * mm});
        }
        {
            var Q0;
            Q0=makeQuery(id+"F52.opExtrude","CAP_FACE",FACE,{"disambiguationData":[OSD([sQuery(id+"F51.wireOp",EDGE,"E68"),sQuery(id+"F51.wireOp",EDGE,"E69")])],"isStart":false});
            var sketch = newSketch(context, id + "F56", { "sketchPlane" : qUnion([Q0])});
            skCircle(sketch, "E72", {"center": v(44.04, -0.12) * mm, "radius": 2.5 * mm});
            skCircle(sketch, "E73", {"center": v(44.04, -0.12) * mm, "radius": 3.88 * mm});
            skSolve(sketch);
        }
        {
            var Q0;
            Q0=qSketchRegion(id+"F56",true);
            extrude(context, id + "F57", {"entities" : qUnion([Q0]), "operationType" : NewBodyOperationType.ADD, "depth" : 1.75 * mm, "offsetDistance" : 25 * mm});
        }
        {
            var Q0;
            Q0=makeQuery(id+"F57.opExtrude","CAP_EDGE",EDGE,{"disambiguationData":[OSD([sQuery(id+"F56.wireOp",EDGE,"E73")])],"isStart":false});
            fillet(context, id + "F58", {"entities" : qUnion([Q0]), "radius" : 0.75 * mm, "tangentPropagation" : true, "allowEdgeOverflow" : false});
        }
        {
            var Q0;
            Q0=qCreatedBy(makeId("Front.planeOp"),FACE);
            var sketch = newSketch(context, id + "F59", { "sketchPlane" : qUnion([Q0])});
            skCircle(sketch, "E74", {"center": v(-44.4, -10.54) * mm, "radius": 2.65 * mm});
            skCircle(sketch, "E75", {"center": v(-44.4, -10.54) * mm, "radius": 5 * mm});
            skSolve(sketch);
        }
        {
            var Q0;
            Q0=qSketchRegion(id+"F59",true);
            extrude(context, id + "F60", {"entities" : qUnion([Q0]), "oppositeDirection" : true, "depth" : 1 * mm, "offsetDistance" : 25 * mm});
        }
        {
            var Q0;
            Q0=qCreatedBy(makeId("Top.planeOp"),FACE);
            var sketch = newSketch(context, id + "F61", { "sketchPlane" : qUnion([Q0])});
            skLineSegment(sketch, "E76", {"start": v(47.6, 27.95) * mm, "end": v(47.6, -4.13) * mm});
            skLineSegment(sketch, "E77", {"start": v(47.6, -4.13) * mm, "end": v(45.86, -4.13) * mm});
            skLineSegment(sketch, "E78", {"start": v(43.9, -2.45) * mm, "end": v(43.9, -2.05) * mm});
            skLineSegment(sketch, "E79", {"start": v(43.9, -2.05) * mm, "end": v(45.6, -2.05) * mm});
            skLineSegment(sketch, "E80", {"start": v(45.6, -2.05) * mm, "end": v(45.6, 27.54) * mm});
            skLineSegment(sketch, "E81", {"start": v(45.6, 27.54) * mm, "end": v(45.97, 27.95) * mm});
            skLineSegment(sketch, "E82", {"start": v(45.97, 27.95) * mm, "end": v(47.6, 27.95) * mm});
            skArc(sketch, "E83", {"start": v(45.86, -4.13) * mm, "mid": v(44.68, -3.53) * mm, "end": v(43.9, -2.45) * mm});
            skSolve(sketch);
        }
        {
            var Q0;
            Q0=makeQuery(id+"F61.imprint","IMPRINT",FACE,{"disambiguationData":[TD([[makeQuery(id+"F61.imprint","IMPRINT",EDGE,{"derivedFrom":sQuery(id+"F61.wireOp",EDGE,"E76")}),-1.0]])]});
            var Q1;
            Q1=sQuery(id+"F61.wireOp",EDGE,"E76");
            revolve(context, id + "F62", {"entities" : qUnion([Q0]), "axis" : qUnion([Q1]), "revolveType" : RevolveType.FULL});
        }
        {
            var Q0;
            Q0=makeQuery(id+"F62.opRevolve","SWEPT_FACE",FACE,{"disambiguationData":[OSD([sQuery(id+"F61.wireOp",EDGE,"E77")])]});
            var sketch = newSketch(context, id + "F63", { "sketchPlane" : qUnion([Q0])});
            skCircle(sketch, "E84.cCircle", {"center": v(47.6, 0) * mm, "radius": 1.25 * mm, "construction": true});
            skLineSegment(sketch, "E84.0", {"start": v(48.97, -0.48) * mm, "end": v(47.87, -1.42) * mm});
            skLineSegment(sketch, "E84.1", {"start": v(47.87, -1.42) * mm, "end": v(46.51, -0.94) * mm});
            skLineSegment(sketch, "E84.2", {"start": v(46.51, -0.94) * mm, "end": v(46.25, 0.48) * mm});
            skLineSegment(sketch, "E84.3", {"start": v(46.25, 0.48) * mm, "end": v(47.35, 1.42) * mm});
            skLineSegment(sketch, "E84.4", {"start": v(47.35, 1.42) * mm, "end": v(48.7, 0.94) * mm});
            skLineSegment(sketch, "E84.5", {"start": v(48.7, 0.94) * mm, "end": v(48.97, -0.48) * mm});
            skPoint(sketch, "E84.0.midPoint", {"position": v(48.42, -0.95) * mm});
            skSolve(sketch);
        }
        {
            var Q0;
            Q0=qSketchRegion(id+"F63",true);
            extrude(context, id + "F64", {"entities" : qUnion([Q0]), "operationType" : NewBodyOperationType.REMOVE, "oppositeDirection" : true, "depth" : 1.3 * mm, "offsetDistance" : 25 * mm});
        }
        {
            var Q0;
            Q0=qCreatedBy(makeId("Front.planeOp"),FACE);
            var sketch = newSketch(context, id + "F65", { "sketchPlane" : qUnion([Q0])});
            skCircle(sketch, "E85", {"center": v(-28.82, -11.06) * mm, "radius": 2.15 * mm});
            skCircle(sketch, "E86", {"center": v(-28.82, -11.06) * mm, "radius": 4.5 * mm});
            skSolve(sketch);
        }
        {
            var Q0;
            Q0=qSketchRegion(id+"F65",true);
            extrude(context, id + "F66", {"entities" : qUnion([Q0]), "depth" : 0.8 * mm, "offsetDistance" : 25 * mm});
        }
        {
            var Q0;
            Q0=qCreatedBy(makeId("Front.planeOp"),FACE);
            var sketch = newSketch(context, id + "F67", { "sketchPlane" : qUnion([Q0])});
            skCircle(sketch, "E87", {"center": v(-0.33, -11.42) * mm, "radius": 3.83 * mm});
            skCircle(sketch, "E88", {"center": v(-0.33, -11.42) * mm, "radius": 2 * mm});
            skSolve(sketch);
        }
        {
            var Q0;
            Q0=qSketchRegion(id+"F67",true);
            extrude(context, id + "F68", {"entities" : qUnion([Q0]), "oppositeDirection" : true, "depth" : 3.25 * mm, "offsetDistance" : 25 * mm});
        }
        {
            var Q0;
            Q0=makeQuery(id+"F68.opExtrude","CAP_EDGE",EDGE,{"disambiguationData":[OSD([sQuery(id+"F67.wireOp",EDGE,"E87")])],"isStart":true});
            var Q1;
            Q1=makeQuery(id+"F68.opExtrude","CAP_EDGE",EDGE,{"disambiguationData":[OSD([sQuery(id+"F67.wireOp",EDGE,"E88")])],"isStart":true});
            var Q2;
            Q2=makeQuery(id+"F68.opExtrude","CAP_EDGE",EDGE,{"disambiguationData":[OSD([sQuery(id+"F67.wireOp",EDGE,"E87")])],"isStart":false});
            chamfer(context, id + "F69", {"entities" : qUnion([Q0, Q1, Q2]), "width" : 0.33 * mm, "tangentPropagation" : true});
        }
        {
            var Q0;
            Q0=makeQuery(id+"F68.opExtrude","CAP_FACE",FACE,{"disambiguationData":[OSD([sQuery(id+"F67.wireOp",EDGE,"E87"),sQuery(id+"F67.wireOp",EDGE,"E88")])],"isStart":false});
            var sketch = newSketch(context, id + "F70", { "sketchPlane" : qUnion([Q0])});
            skCircle(sketch, "E89", {"center": v(0.33, -11.42) * mm, "radius": 3.5 * mm});
            skSolve(sketch);
        }
        {
            var Q0;
            Q0=qSketchRegion(id+"F70",true);
            extrude(context, id + "F71", {"entities" : qUnion([Q0]), "operationType" : NewBodyOperationType.ADD, "depth" : 4.75 * mm, "offsetDistance" : 25 * mm});
        }
        {
            var Q0;
            Q0=makeQuery(id+"F71.opExtrude","CAP_EDGE",EDGE,{"disambiguationData":[OSD([sQuery(id+"F70.wireOp",EDGE,"E89")])],"isStart":false});
            fillet(context, id + "F72", {"entities" : qUnion([Q0]), "radius" : 3.5 * mm, "tangentPropagation" : true, "allowEdgeOverflow" : false});
        }
        {
            var Q0;
            Q0=makeQuery(id+"F68.opExtrude","CAP_FACE",FACE,{"disambiguationData":[OSD([sQuery(id+"F67.wireOp",EDGE,"E87"),sQuery(id+"F67.wireOp",EDGE,"E88")])],"isStart":true});
            var sketch = newSketch(context, id + "F73", { "sketchPlane" : qUnion([Q0])});
            skCircle(sketch, "E90.cCircle", {"center": v(-0.33, -11.42) * mm, "radius": 3.5 * mm, "construction": true});
            skLineSegment(sketch, "E90.0", {"start": v(3.17, -9.4) * mm, "end": v(3.17, -13.44) * mm});
            skLineSegment(sketch, "E90.1", {"start": v(3.17, -13.44) * mm, "end": v(-0.33, -15.47) * mm});
            skLineSegment(sketch, "E90.2", {"start": v(-0.33, -15.47) * mm, "end": v(-3.83, -13.44) * mm});
            skLineSegment(sketch, "E90.3", {"start": v(-3.83, -13.44) * mm, "end": v(-3.83, -9.4) * mm});
            skLineSegment(sketch, "E90.4", {"start": v(-3.83, -9.4) * mm, "end": v(-0.33, -7.38) * mm});
            skLineSegment(sketch, "E90.5", {"start": v(-0.33, -7.38) * mm, "end": v(3.17, -9.4) * mm});
            skPoint(sketch, "E90.0.midPoint", {"position": v(3.17, -11.42) * mm});
            skCircle(sketch, "E91", {"center": v(-0.33, -11.42) * mm, "radius": 6.02 * mm});
            skSolve(sketch);
        }
        {
            var Q0;
            Q0=qSketchRegion(id+"F73",true);
            extrude(context, id + "F74", {"entities" : qUnion([Q0]), "operationType" : NewBodyOperationType.REMOVE, "oppositeDirection" : true, "depth" : 25 * mm, "offsetDistance" : 25 * mm});
        }
        {
            var Q0;
            Q0=qCreatedBy(makeId("Front.planeOp"),FACE);
            var sketch = newSketch(context, id + "F75", { "sketchPlane" : qUnion([Q0])});
            skCircle(sketch, "E92", {"center": v(-14.67, -11.95) * mm, "radius": 6 * mm});
            skCircle(sketch, "E93", {"center": v(-14.67, -11.95) * mm, "radius": 2.08 * mm});
            skSolve(sketch);
        }
        {
            var Q0;
            Q0 = qSketchRegion(id + "F75", true);
            extrude(context, id + "F76", {"entities" : qUnion([Q0]), "depth" : 0.5 * mm, "offsetDistance" : 25 * mm, "hasSecondDirection" : true, "secondDirectionOppositeDirection" : true, "secondDirectionDepth" : 2.5 * mm});
        }
        {
            var Q0;
            Q0=qCreatedBy(makeId("Front.planeOp"),FACE);
            var sketch = newSketch(context, id + "F77", { "sketchPlane" : qUnion([Q0])});
            skCircle(sketch, "E94", {"center": v(-14.67, -11.95) * mm, "radius": 4 * mm});
            skSolve(sketch);
        }
        {
            var Q0;
            Q0 = qSketchRegion(id + "F77", true);
            extrude(context, id + "F78", {"entities" : qUnion([Q0]), "operationType" : NewBodyOperationType.REMOVE, "oppositeDirection" : true, "depth" : 25 * mm, "offsetDistance" : 25 * mm, "hasDraft" : true, "draftAngle" : 45 * degree, "draftPullDirection" : true, "hasSecondDirection" : true, "secondDirectionOppositeDirection" : false, "secondDirectionDepth" : 25 * mm});
        }
        {
            var Q0;
            Q0=makeQuery(id+"F76.opExtrude","CAP_EDGE",EDGE,{"disambiguationData":[OSD([sQuery(id+"F75.wireOp",EDGE,"E92")])],"isStart":false});
            var Q1;
            Q1=makeQuery(id+"F76.opExtrude","CAP_EDGE",EDGE,{"disambiguationData":[OSD([sQuery(id+"F75.wireOp",EDGE,"E92")])],"isStart":true});
            chamfer(context, id + "F79", {"entities" : qUnion([Q0, Q1]), "width" : 0.2 * mm, "tangentPropagation" : true});
        }
        {
            var Q0;
            Q0=qCreatedBy(makeId("Top.planeOp"),FACE);
            var sketch = newSketch(context, id + "F80", { "sketchPlane" : qUnion([Q0])});
            skLineSegment(sketch, "E95", {"start": v(93, -8.73) * mm, "end": v(89.2, -8.73) * mm});
            skLineSegment(sketch, "E96", {"start": v(89.2, -8.73) * mm, "end": v(89.2, -8.23) * mm});
            skLineSegment(sketch, "E97", {"start": v(89.2, -8.23) * mm, "end": v(91, -6.43) * mm});
            skLineSegment(sketch, "E98", {"start": v(91, -6.43) * mm, "end": v(91, 18.22) * mm});
            skLineSegment(sketch, "E99", {"start": v(91, 18.22) * mm, "end": v(91.36, 18.57) * mm});
            skLineSegment(sketch, "E100", {"start": v(91.36, 18.57) * mm, "end": v(93, 18.57) * mm});
            skLineSegment(sketch, "E101", {"start": v(93, 18.57) * mm, "end": v(93, -8.73) * mm});
            skSolve(sketch);
        }
        {
            var Q0;
            Q0 = qSketchRegion(id + "F80", true);
            var Q1;
            Q1=sQuery(id+"F80.wireOp",EDGE,"E101");
            revolve(context, id + "F81", {"entities" : qUnion([Q0]), "axis" : qUnion([Q1]), "revolveType" : RevolveType.FULL});
        }
        {
            var Q0;
            Q0=makeQuery(id+"F81.opRevolve","SWEPT_FACE",FACE,{"disambiguationData":[OSD([sQuery(id+"F80.wireOp",EDGE,"E95")])]});
            var sketch = newSketch(context, id + "F82", { "sketchPlane" : qUnion([Q0])});
            skCircle(sketch, "E102.cCircle", {"center": v(93, 0) * mm, "radius": 1.25 * mm, "construction": true});
            skLineSegment(sketch, "E102.0", {"start": v(92.74, 1.42) * mm, "end": v(94.1, 0.94) * mm});
            skLineSegment(sketch, "E102.1", {"start": v(94.1, 0.94) * mm, "end": v(94.36, -0.48) * mm});
            skLineSegment(sketch, "E102.2", {"start": v(94.36, -0.48) * mm, "end": v(93.27, -1.42) * mm});
            skLineSegment(sketch, "E102.3", {"start": v(93.27, -1.42) * mm, "end": v(91.9, -0.94) * mm});
            skLineSegment(sketch, "E102.4", {"start": v(91.9, -0.94) * mm, "end": v(91.64, 0.48) * mm});
            skLineSegment(sketch, "E102.5", {"start": v(91.64, 0.48) * mm, "end": v(92.74, 1.42) * mm});
            skPoint(sketch, "E102.0.midPoint", {"position": v(93.42, 1.18) * mm});
            skSolve(sketch);
        }
        {
            var Q0;
            Q0 = qSketchRegion(id + "F82", true);
            extrude(context, id + "F83", {"entities" : qUnion([Q0]), "operationType" : NewBodyOperationType.REMOVE, "oppositeDirection" : true, "depth" : 1.8 * mm, "offsetDistance" : 25 * mm});
        }
    });
